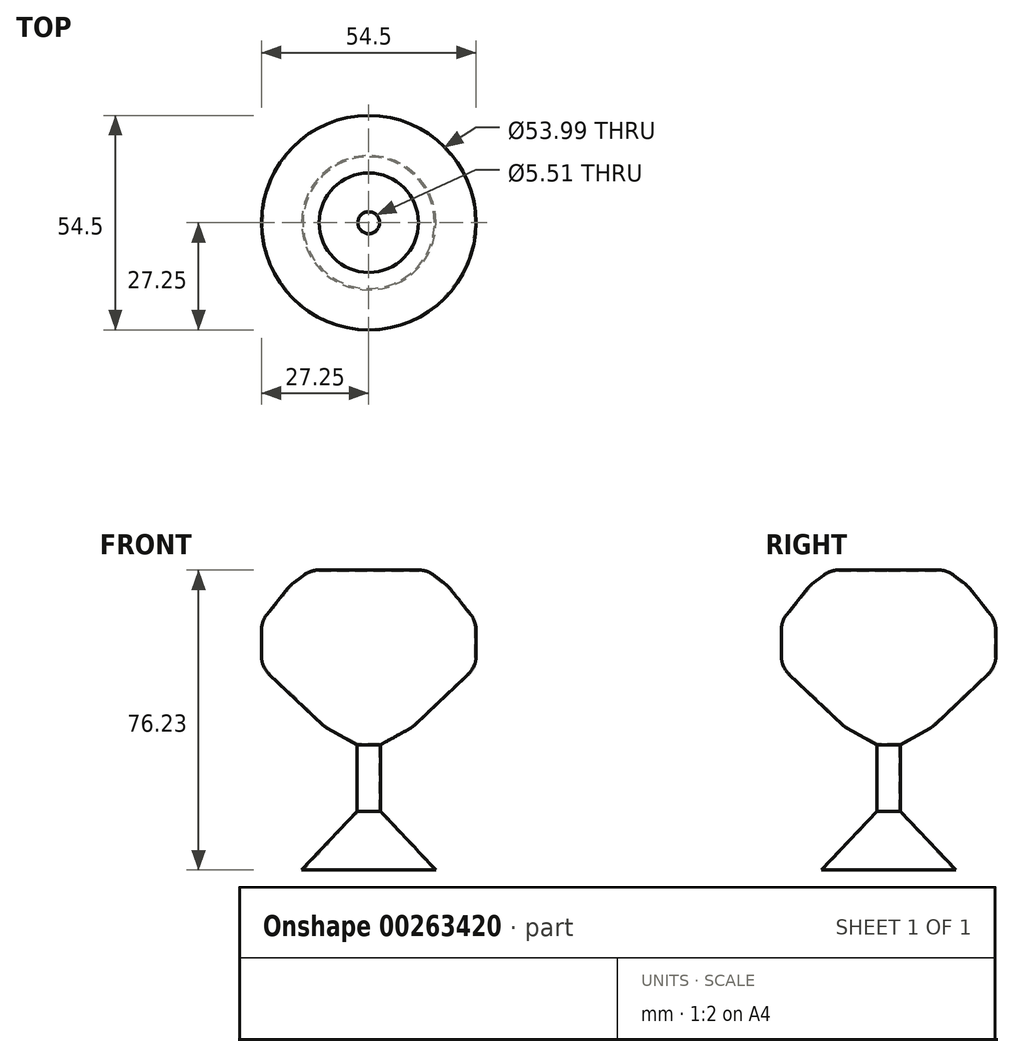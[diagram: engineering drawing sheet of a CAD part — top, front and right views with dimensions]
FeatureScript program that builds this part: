
annotation { "Feature Type Name" : "Feature", "Feature Type Description" : "" }
export const myFeature = defineFeature(function(context is Context, id is Id, definition is map)
    precondition{}
    {
        {
            var Q0;
            Q0=qCreatedBy(makeId("Front.planeOp"),FACE);
            var sketch = newSketch(context, id + "F0", { "sketchPlane" : qUnion([Q0])});
            skLineSegment(sketch, "E0", {"start": v(0, 0) * mm, "end": v(0, 76.06) * mm, "construction": true});
            skLineSegment(sketch, "E1", {"start": v(-3.01, 14.95) * mm, "end": v(-3.01, 31.86) * mm});
            skLineSegment(sketch, "E2", {"start": v(-3.01, 31.86) * mm, "end": v(-10.44, 35.94) * mm});
            skLineSegment(sketch, "E3", {"start": v(-11.75, 36.9) * mm, "end": v(-25.27, 49.74) * mm});
            skLineSegment(sketch, "E4", {"start": v(-27.25, 54.34) * mm, "end": v(-27.25, 61) * mm});
            skLineSegment(sketch, "E5", {"start": v(-25.87, 64.96) * mm, "end": v(-20.6, 71.58) * mm});
            skLineSegment(sketch, "E6", {"start": v(-19.5, 72.66) * mm, "end": v(-16.58, 74.91) * mm});
            skLineSegment(sketch, "E7", {"start": v(-12.62, 76.23) * mm, "end": v(0, 76.06) * mm});
            skPoint(sketch, "E8.visualSharp", {"position": v(-27.25, 63.22) * mm});
            skArc(sketch, "E8.filletArc", {"start": v(-25.87, 64.96) * mm, "mid": v(-26.9, 63.1) * mm, "end": v(-27.25, 61) * mm});
            skPoint(sketch, "E9.visualSharp", {"position": v(-20.12, 72.19) * mm});
            skArc(sketch, "E9.filletArc", {"start": v(-19.5, 72.66) * mm, "mid": v(-20.09, 72.15) * mm, "end": v(-20.6, 71.58) * mm});
            skPoint(sketch, "E10.visualSharp", {"position": v(-14.83, 76.26) * mm});
            skArc(sketch, "E10.filletArc", {"start": v(-12.62, 76.23) * mm, "mid": v(-14.7, 75.9) * mm, "end": v(-16.58, 74.91) * mm});
            skLineSegment(sketch, "E11", {"start": v(-17.07, 0) * mm, "end": v(0, 0) * mm});
            skLineSegment(sketch, "E12", {"start": v(0, 76.06) * mm, "end": v(0, 0) * mm});
            skLineSegment(sketch, "E13", {"start": v(-3.01, 14.95) * mm, "end": v(-17.07, 0) * mm});
            skPoint(sketch, "E14.visualSharp", {"position": v(-27.25, 51.61) * mm});
            skArc(sketch, "E14.filletArc", {"start": v(-27.25, 54.34) * mm, "mid": v(-26.73, 51.83) * mm, "end": v(-25.27, 49.74) * mm});
            skPoint(sketch, "E15.visualSharp", {"position": v(-11.16, 36.34) * mm});
            skArc(sketch, "E15.filletArc", {"start": v(-11.75, 36.9) * mm, "mid": v(-11.13, 36.38) * mm, "end": v(-10.44, 35.94) * mm});
            skSolve(sketch);
        }
        {
            var Q0;
            Q0=makeQuery(id+"F0.imprint","IMPRINT",FACE,{"disambiguationData":[TD([[makeQuery(id+"F0.imprint","IMPRINT",EDGE,{"derivedFrom":sQuery(id+"F0.wireOp",EDGE,"BMc201qQ-0je7-Gwoe-EpYM-bDg0XFheS4Df")}),-1.0]])]});
            var Q1;
            Q1=makeQuery(id+"F0.imprint","IMPRINT",FACE,{"disambiguationData":[TD([[makeQuery(id+"F0.imprint","IMPRINT",EDGE,{"derivedFrom":sQuery(id+"F0.wireOp",EDGE,"E1")}),-1.0]])]});
            var Q2;
            Q2=sQuery(id+"F0.wireOp",EDGE,"E12");
            revolve(context, id + "F1", {"entities" : qUnion([Q0, Q1]), "axis" : qUnion([Q2]), "revolveType" : RevolveType.FULL});
        }
        {
            var Q0;
            Q0=makeQuery(id+"F1.opRevolve","SWEPT_FACE",FACE,{"disambiguationData":[OSD([sQuery(id+"F0.wireOp",EDGE,"E7")])]});
            var Q1;
            Q1=makeQuery(id+"F1.opRevolve","SWEPT_FACE",FACE,{"disambiguationData":[OSD([sQuery(id+"F0.wireOp",EDGE,"E11")])]});
            var Q2;
            Q2=makeQuery(id+"F1.opRevolve","SWEPT_BODY",BODY,{"disambiguationData":[OSD([sQuery(id+"F0.wireOp",EDGE,"BMc201qQ-0je7-Gwoe-EpYM-bDg0XFheS4Df"),sQuery(id+"F0.wireOp",EDGE,"E1"),sQuery(id+"F0.wireOp",EDGE,"E2"),sQuery(id+"F0.wireOp",EDGE,"E3"),sQuery(id+"F0.wireOp",EDGE,"E4"),sQuery(id+"F0.wireOp",EDGE,"E5"),sQuery(id+"F0.wireOp",EDGE,"E6"),sQuery(id+"F0.wireOp",EDGE,"E7"),sQuery(id+"F0.wireOp",EDGE,"E8.filletArc"),sQuery(id+"F0.wireOp",EDGE,"E9.filletArc"),sQuery(id+"F0.wireOp",EDGE,"E10.filletArc"),sQuery(id+"F0.wireOp",EDGE,"E11"),sQuery(id+"F0.wireOp",EDGE,"E12")])]});
            shell(context, id + "F2", {"entities" : qUnion([Q0, Q1]), "parts" : qUnion([Q2]), "thickness" : 0.25 * mm});
        }
    });
